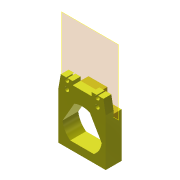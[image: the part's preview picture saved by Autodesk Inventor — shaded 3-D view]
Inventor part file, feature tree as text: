
AUTODESK INVENTOR PART (.ipt)
format: ipt  version: 2019.4 (Build 234330000, 330)  size: 202,240 bytes
history: native  units: mm
features: extrude x5, reference x5, other x5, sketch x4, projected_geometry x2, plane x1
ambient origin geometry x8: Origin, YZ Plane, XZ Plane, XY Plane, X Axis, Y Axis, Z Axis, Center Point
bodies: Solid1 (feature_tree)
feature tree (22):
  plane  "Work Plane1"
  extrude  "Extrusion1"  Depth=30.0mm
  extrude  "Extrusion2"  Depth=5.0mm TaperAngle=0.0deg
  extrude  "Extrusion4"  Depth=5.0mm TaperAngle=0.0deg
  extrude  "Extrusion5"  Depth=5.0mm TaperAngle=0.0deg
  extrude  "Extrusion6"  Depth=5.0mm TaperAngle=0.0deg
  sketch  "Sketch1"  dims[d0=25.0mm d1=30.0mm]
  reference  "Reference1"
  reference  "Reference2"
  sketch  "Sketch2"  dims[d2=30.0mm d3=5.0mm d4=0.0mm]
  reference  "Reference3"
  reference  "Reference4"
  reference  "Reference5"
  projected_geometry  "Projected Loop1"
  sketch  "Sketch4"  dims[d5=20.0mm d6=5.0mm d7=0.0mm]
  sketch  "Sketch5"  dims[d10=5.0mm d11=0.0mm d12=1.0mm d13=0.0mm d14=1.0mm d15=0.0mm]
  projected_geometry  "Projected Loop2"
  other  "Assembly_Cube_Z_Focus_MGN_NEMA_v3.iam"
  other  "30_Cube_Z_Focus_MGN_NEMA_slide:1"
  other  "00_Microscope_Objective_Lens10x:1"
  other  "Assembly_Cube_empty_IM_v3:2"
  other  "10_Cube_1x1_IM:1"
